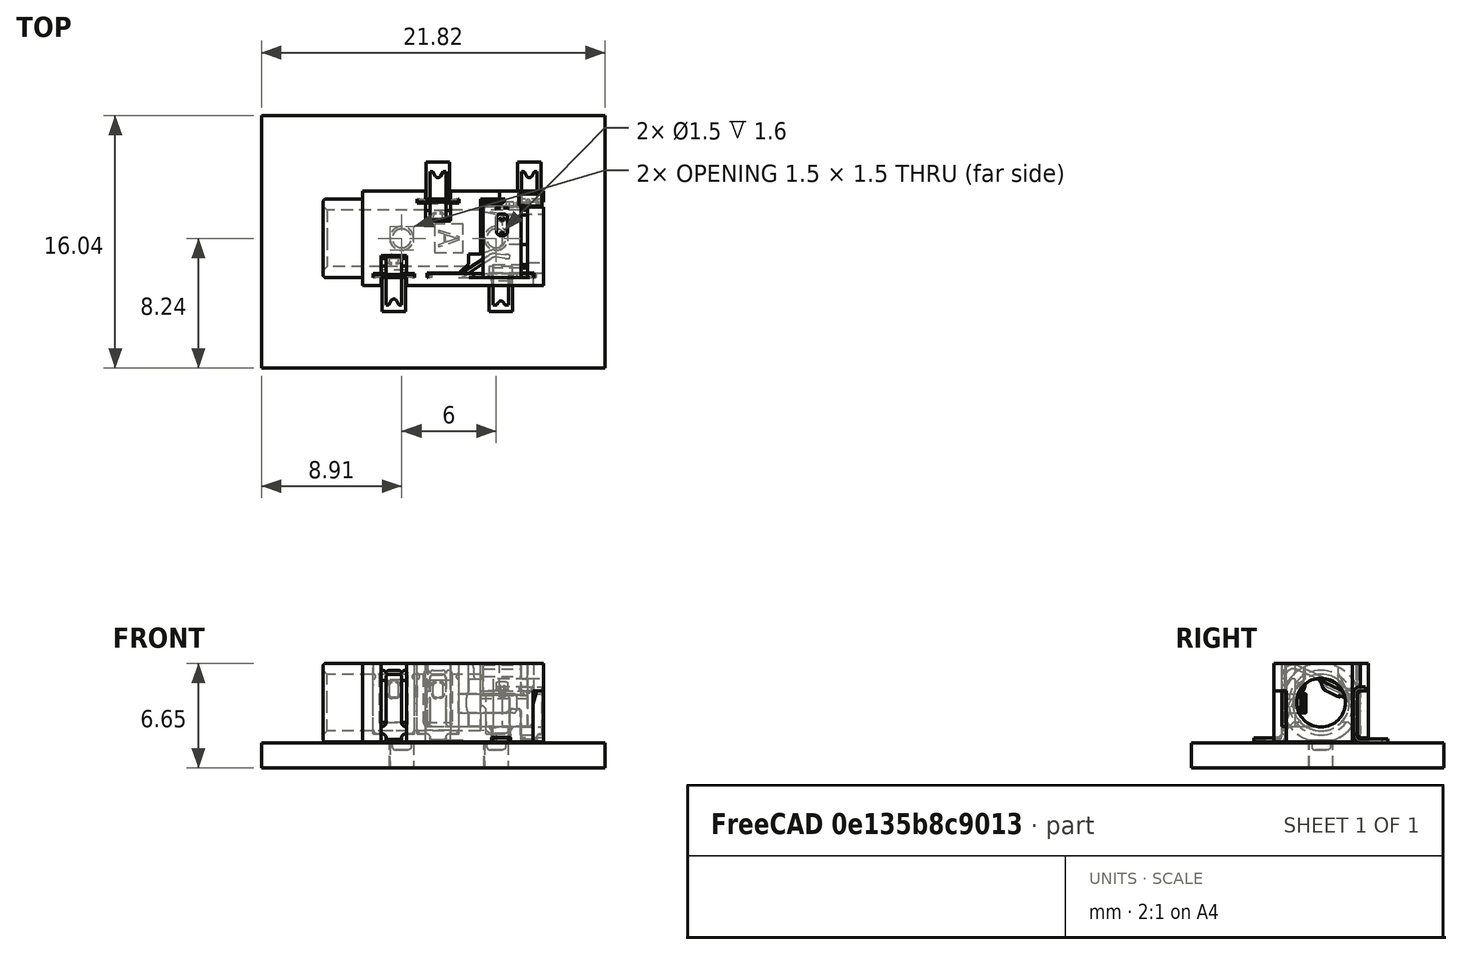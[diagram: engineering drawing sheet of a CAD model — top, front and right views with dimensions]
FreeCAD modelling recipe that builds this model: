
FCSTD DOCUMENT  (FreeCAD 0.21R33694 (Git))
Label: CUI_SJ2-35813B-SMT-TR
License: All rights reserved
LicenseURL: https://en.wikipedia.org/wiki/All_rights_reserved
objects: Part::Feature×8, Sketcher::SketchObject×3, Part::Compound×1, App::DocumentObjectGroup×1
note: 12 computed .brp shape members not serialized (recipe doc carries the construction recipe); baked Part::Feature solids carry a one-line shape summary decoded from their .brp

FEATURE [Part::Feature] anr_  label="drill_000"
  shape: bbox 1.52 x 1.52 x 1.6 mm, 4 faces (baked)
FEATURE [Part::Feature] anr_001  label="drill_001"
  shape: bbox 1.52 x 1.52 x 1.6 mm, 4 faces (baked)
FEATURE [Part::Compound] annulars  label="TH-Drills"
  Links = -> [anr_,anr_001]
FEATURE [Part::Feature] Shape001  label="topPads"
  Placement = pos=(0,0,-0.01) rot=(0,0,1;0rad)
  shape: bbox 10.1 x 9.5 x 0.01 mm, 24 faces, 4 solids (baked)
FEATURE [Part::Feature] Shape  label="F.SilkS_outline_"
  Placement = pos=(0,0,0.01) rot=(0,0,1;0rad)
  shape: bbox 11.63 x 8.633 x 2e-07 mm, 0 faces, 0 solids (baked)
FEATURE [Sketcher::SketchObject] _F_SilkS__sketch  label="F.SilkS_"
  FullyConstrained = false
  Placement = pos=(0,0,0.01) rot=(0,0,1;0rad)
  sketch-geometry (8):
    g0: LineSegment StartX=-5.75 StartY=-3 StartZ=0 EndX=-5.75 EndY=3 EndZ=0
    g1: LineSegment StartX=-5.75 StartY=3 StartZ=0 EndX=-2.1 EndY=3 EndZ=0
    g2: LineSegment StartX=0.2 StartY=3 StartZ=0 EndX=3.55 EndY=3 EndZ=0
    g3: LineSegment StartX=5.75 StartY=1.7 StartZ=0 EndX=5.75 EndY=-3 EndZ=0
    g4: LineSegment StartX=5.75 StartY=-3 StartZ=0 EndX=4.25 EndY=-3 EndZ=0
    g5: LineSegment StartX=1.75 StartY=-3 StartZ=0 EndX=-2.55 EndY=-3 EndZ=0
    g6: LineSegment StartX=-5 StartY=-3 StartZ=0 EndX=-5.75 EndY=-3 EndZ=0
    g7: Circle CenterX=-3.75 CenterY=-5.369 CenterZ=0 NormalX=0 NormalY=0 NormalZ=1 AngleXU=0 Radius=0.1
FEATURE [Part::Feature] Shape002  label="F.CrtYd_outline_"
  Placement = pos=(0,0,0.01) rot=(0,0,1;0rad)
  shape: bbox 14.55 x 10.05 x 2e-07 mm, 0 faces, 0 solids (baked)
FEATURE [Sketcher::SketchObject] _F_CrtYd__sketch  label="F.CrtYd_"
  FullyConstrained = false
  Placement = pos=(0,0,0.01) rot=(0,0,1;0rad)
  sketch-geometry (4):
    g0: LineSegment StartX=-8.5 StartY=5.1 StartZ=0 EndX=6 EndY=5.1 EndZ=0
    g1: LineSegment StartX=6 StartY=5.1 StartZ=0 EndX=6 EndY=-4.9 EndZ=0
    g2: LineSegment StartX=6 StartY=-4.9 StartZ=0 EndX=-8.5 EndY=-4.9 EndZ=0
    g3: LineSegment StartX=-8.5 StartY=-4.9 StartZ=0 EndX=-8.5 EndY=5.1 EndZ=0
FEATURE [Part::Feature] Shape003  label="F.Fab_outline_"
  Placement = pos=(0,0,0.01) rot=(0,0,1;0rad)
  shape: bbox 14.13 x 8.633 x 2e-07 mm, 0 faces, 0 solids (baked)
FEATURE [Sketcher::SketchObject] _F_Fab__sketch  label="F.Fab_"
  FullyConstrained = false
  Placement = pos=(0,0,0.01) rot=(0,0,1;0rad)
  sketch-geometry (10):
    g0: LineSegment StartX=-5.75 StartY=3 StartZ=0 EndX=5.75 EndY=3 EndZ=0
    g1: LineSegment StartX=5.75 StartY=3 StartZ=0 EndX=5.75 EndY=-3 EndZ=0
    g2: LineSegment StartX=5.75 StartY=-3 StartZ=0 EndX=-5.75 EndY=-3 EndZ=0
    g3: LineSegment StartX=-5.75 StartY=-3 StartZ=0 EndX=-5.75 EndY=-2.5 EndZ=0
    g4: LineSegment StartX=-5.75 StartY=-2.5 StartZ=0 EndX=-5.75 EndY=2.5 EndZ=0
    g5: LineSegment StartX=-5.75 StartY=2.5 StartZ=0 EndX=-5.75 EndY=3 EndZ=0
    g6: LineSegment StartX=-5.75 StartY=2.5 StartZ=0 EndX=-8.25 EndY=2.5 EndZ=0
    g7: LineSegment StartX=-8.25 StartY=2.5 StartZ=0 EndX=-8.25 EndY=-2.5 EndZ=0
    g8: LineSegment StartX=-8.25 StartY=-2.5 StartZ=0 EndX=-5.75 EndY=-2.5 EndZ=0
    g9: Circle CenterX=-3.75 CenterY=-5.369 CenterZ=0 NormalX=0 NormalY=0 NormalZ=1 AngleXU=0 Radius=0.1
FEATURE [Part::Feature] PCB
  shape: bbox 21.83 x 16.04 x 1.58 mm, 10 faces (baked)
FEATURE [App::DocumentObjectGroup] Group  label="CUI_SJ2-35813B-SMT-TR-fp"
  Group = -> [Shape001,annulars,_F_SilkS__sketch,Shape,_F_CrtYd__sketch,Shape002,_F_Fab__sketch,Shape003,PCB]
FEATURE [Part::Feature] Shape094  label="CUI_DEVICES_SJ2-35813B-SMT-TR"
  shape: bbox 14 x 8.5 x 5.706 mm, 521 faces (baked)
